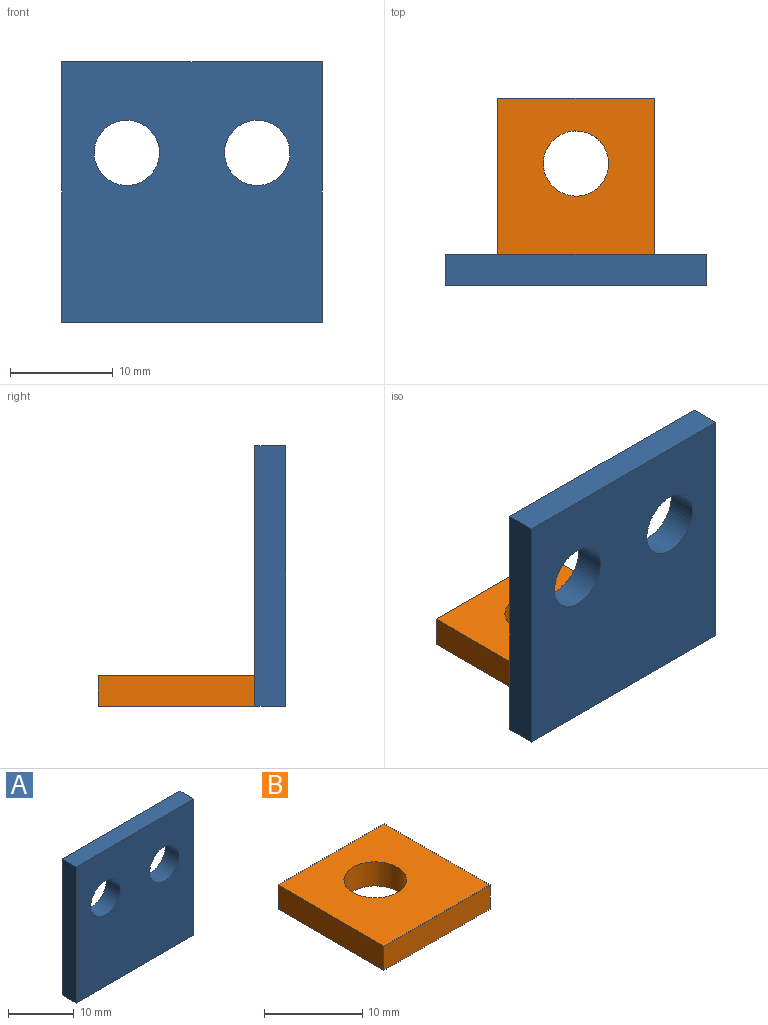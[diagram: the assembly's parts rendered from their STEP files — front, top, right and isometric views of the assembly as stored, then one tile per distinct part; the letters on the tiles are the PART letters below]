
ASSEMBLY  parts=2 mates=1
PART A: 8 faces, bbox 25.4x3x25.4 mm
  f0: plane 25.4x3mm, normal (0,0,1), area 76.2mm2, adj f1,f5,f6,f7
  f1: plane 25.4x3mm, normal (-1,0,0), area 76.2mm2, adj f0,f2,f6,f7
  f2: plane 25.4x3mm, normal (0,0,-1), area 76.2mm2, adj f1,f5,f6,f7
  f3: cylinder r=3.17mm len=6.35mm, axis (0,1,0), area 59.8mm2, adj f6,f7
  f4: cylinder r=3.17mm len=6.35mm, axis (0,1,0), area 59.8mm2, adj f6,f7
  f5: plane 25.4x3mm, normal (1,0,0), area 76.2mm2, adj f0,f2,f6,f7
  f6: plane 25.4x25.4mm, normal (0,-1,0), area 581.8mm2, adj f0,f1,f2,f3,f4,f5
  f7: plane 25.4x25.4mm, normal (0,1,0), area 581.8mm2, adj f0,f1,f2,f3,f4,f5
PART B: 7 faces, bbox 15.2x15.2x3 mm
  f0: plane 15.24x3mm, normal (1,0,0), area 45.7mm2, adj f1,f3,f5,f6
  f1: plane 15.24x3mm, normal (0,1,0), area 45.7mm2, adj f0,f2,f5,f6
  f2: plane 15.24x3mm, normal (-1,0,0), area 45.7mm2, adj f1,f3,f5,f6
  f3: plane 15.24x3mm, normal (0,-1,0), area 45.7mm2, adj f0,f2,f5,f6
  f4: cylinder r=3.17mm len=6.35mm, axis (0,0,-1), area 59.8mm2, adj f5,f6
  f5: plane 15.24x15.24mm, normal (0,0,1), area 200.6mm2, adj f0,f1,f2,f3,f4
  f6: plane 15.24x15.24mm, normal (0,0,-1), area 200.6mm2, adj f0,f1,f2,f3,f4
PLACE A t=(-0.37,-2.41,3.75)mm
PLACE B t=(-0.81,-2.41,3.75)mm
MATE parallel B.f6 <-> A.f2  axis (0,0,-1) through (-0.81,-2.41,3.75)mm
